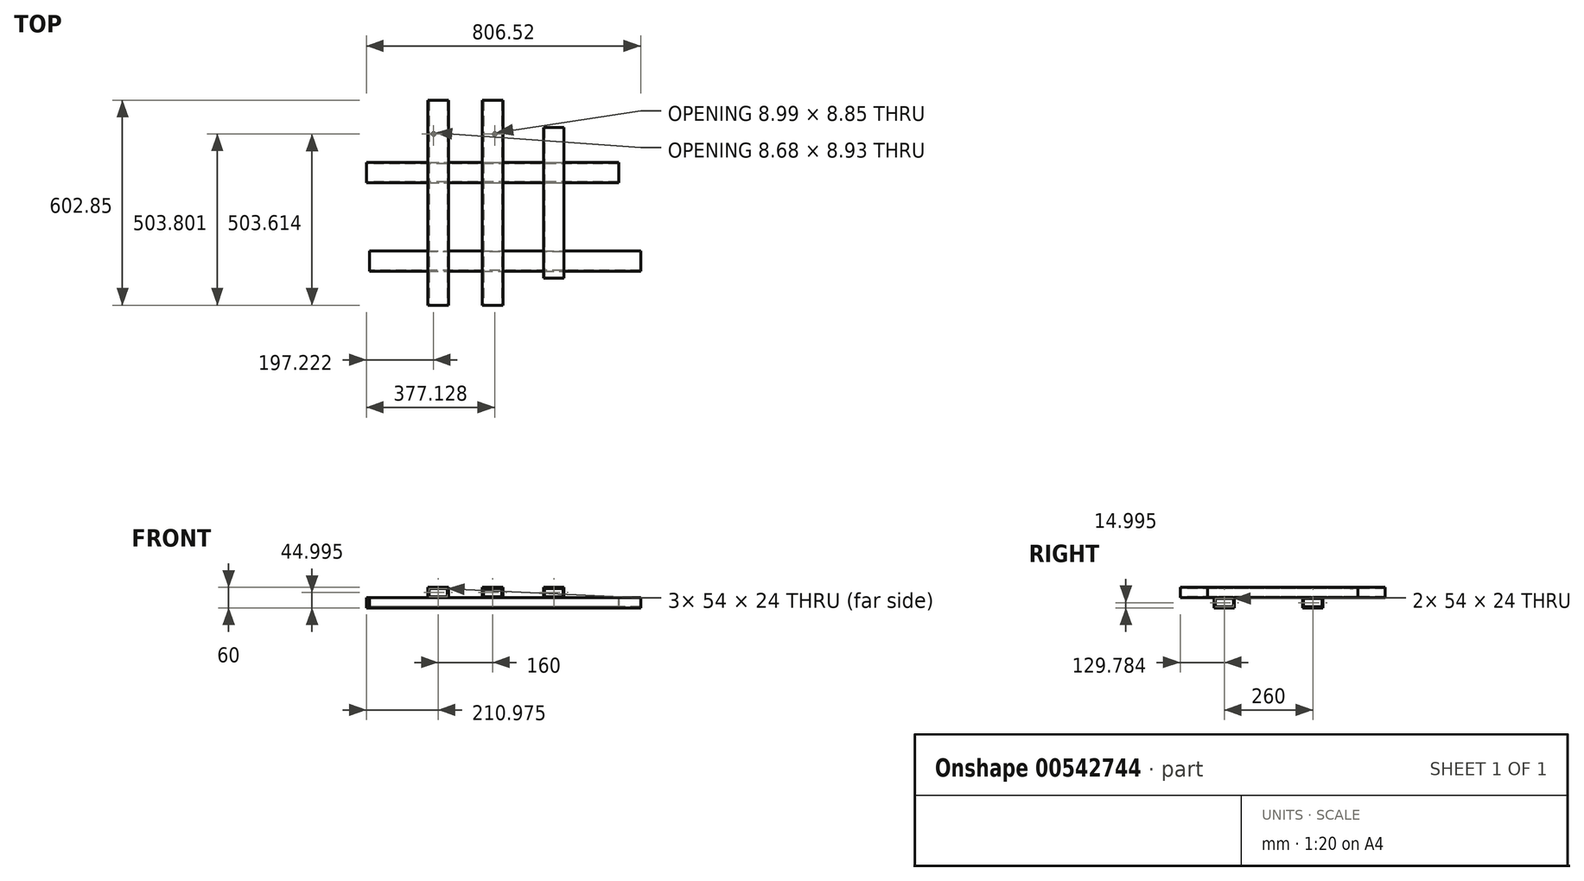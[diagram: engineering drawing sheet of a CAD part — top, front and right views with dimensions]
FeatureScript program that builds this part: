
annotation { "Feature Type Name" : "Feature", "Feature Type Description" : "" }
export const myFeature = defineFeature(function(context is Context, id is Id, definition is map)
    precondition{}
    {
        {
            var Q0;
            Q0=qCreatedBy(makeId("Right.planeOp"),FACE);
            var sketch = newSketch(context, id + "F0", { "sketchPlane" : qUnion([Q0])});
            skLineSegment(sketch, "E0.bottom", {"start": v(-56.7, 72.5) * mm, "end": v(3.3, 72.5) * mm});
            skLineSegment(sketch, "E0.top", {"start": v(-56.7, 42.5) * mm, "end": v(3.3, 42.5) * mm});
            skLineSegment(sketch, "E0.left", {"start": v(-56.7, 72.5) * mm, "end": v(-56.7, 42.5) * mm});
            skLineSegment(sketch, "E0.right", {"start": v(3.3, 72.5) * mm, "end": v(3.3, 42.5) * mm});
            skSolve(sketch);
        }
        {
            var Q0;
            Q0=makeQuery(id+"F0.imprint","IMPRINT",FACE,{"disambiguationData":[TD([[makeQuery(id+"F0.imprint","IMPRINT",EDGE,{"derivedFrom":sQuery(id+"F0.wireOp",EDGE,"E0.bottom")}),-1.0]])]});
            extrude(context, id + "F1", {"entities" : qUnion([Q0]), "depth" : 158 * mm, "offsetDistance" : 25 * mm});
        }
        {
            var Q0;
            Q0=makeQuery(id+"F1.opExtrude","SWEPT_FACE",FACE,{"disambiguationData":[OSD([sQuery(id+"F0.wireOp",EDGE,"E0.left")])]});
            var sketch = newSketch(context, id + "F2", { "sketchPlane" : qUnion([Q0])});
            skLineSegment(sketch, "E1", {"start": v(-144.22, -87.6) * mm, "end": v(237.73, -87.6) * mm, "construction": true});
            skLineSegment(sketch, "E2.bottom", {"start": v(-88.45, -87.6) * mm, "end": v(-22.16, -87.6) * mm});
            skLineSegment(sketch, "E2.top", {"start": v(-88.45, -58.13) * mm, "end": v(-22.16, -58.13) * mm});
            skLineSegment(sketch, "E2.left", {"start": v(-88.45, -87.6) * mm, "end": v(-88.45, -58.13) * mm});
            skLineSegment(sketch, "E2.right", {"start": v(-22.16, -87.6) * mm, "end": v(-22.16, -58.13) * mm});
            skLineSegment(sketch, "E3.bottom", {"start": v(22.03, -87.6) * mm, "end": v(90.42, -87.6) * mm});
            skLineSegment(sketch, "E3.top", {"start": v(22.03, -57.08) * mm, "end": v(90.42, -57.08) * mm});
            skLineSegment(sketch, "E3.left", {"start": v(22.03, -87.6) * mm, "end": v(22.03, -57.08) * mm});
            skLineSegment(sketch, "E3.right", {"start": v(90.42, -87.6) * mm, "end": v(90.42, -57.08) * mm});
            skLineSegment(sketch, "E4.bottom", {"start": v(148.3, -87.6) * mm, "end": v(215.64, -87.6) * mm});
            skLineSegment(sketch, "E4.top", {"start": v(148.3, -57.08) * mm, "end": v(215.64, -57.08) * mm});
            skLineSegment(sketch, "E4.left", {"start": v(148.3, -87.6) * mm, "end": v(148.3, -57.08) * mm});
            skLineSegment(sketch, "E4.right", {"start": v(215.64, -87.6) * mm, "end": v(215.64, -57.08) * mm});
            skSolve(sketch);
        }
        {
            var Q0;
            Q0=makeQuery(id+"F2.imprint","IMPRINT",FACE,{"disambiguationData":[TD([[makeQuery(id+"F2.imprint","IMPRINT",EDGE,{"derivedFrom":sQuery(id+"F2.wireOp",EDGE,"E2.bottom")}),1.0]])]});
            var Q1;
            Q1=makeQuery(id+"F2.imprint","IMPRINT",FACE,{"disambiguationData":[TD([[makeQuery(id+"F2.imprint","IMPRINT",EDGE,{"derivedFrom":sQuery(id+"F2.wireOp",EDGE,"E3.bottom")}),1.0]])]});
            var Q2;
            Q2=makeQuery(id+"F2.imprint","IMPRINT",FACE,{"disambiguationData":[TD([[makeQuery(id+"F2.imprint","IMPRINT",EDGE,{"derivedFrom":sQuery(id+"F2.wireOp",EDGE,"E4.bottom")}),1.0]])]});
            extrude(context, id + "F3", {"entities" : qUnion([Q0, Q1, Q2]), "oppositeDirection" : true, "depth" : 300 * mm, "offsetDistance" : 25 * mm});
        }
        {
            var Q0;
            Q0=makeQuery(id+"F3.opExtrude","SWEPT_FACE",FACE,{"disambiguationData":[OSD([sQuery(id+"F2.wireOp",EDGE,"E2.left")])]});
            var sketch = newSketch(context, id + "F4", { "sketchPlane" : qUnion([Q0])});
            skLineSegment(sketch, "E5.bottom", {"start": v(-213, -87.6) * mm, "end": v(-165.96, -87.6) * mm});
            skLineSegment(sketch, "E5.top", {"start": v(-213, -110.35) * mm, "end": v(-165.96, -110.35) * mm});
            skLineSegment(sketch, "E5.left", {"start": v(-213, -87.6) * mm, "end": v(-213, -110.35) * mm});
            skLineSegment(sketch, "E5.right", {"start": v(-165.96, -87.6) * mm, "end": v(-165.96, -110.35) * mm});
            skLineSegment(sketch, "E6.bottom", {"start": v(-38.67, -87.6) * mm, "end": v(10.72, -87.6) * mm});
            skLineSegment(sketch, "E6.top", {"start": v(-38.67, -111.4) * mm, "end": v(10.72, -111.4) * mm});
            skLineSegment(sketch, "E6.left", {"start": v(-38.67, -87.6) * mm, "end": v(-38.67, -111.4) * mm});
            skLineSegment(sketch, "E6.right", {"start": v(10.72, -87.6) * mm, "end": v(10.72, -111.4) * mm});
            skSolve(sketch);
        }
        {
            var Q0;
            Q0=makeQuery(id+"F4.imprint","IMPRINT",FACE,{"disambiguationData":[TD([[makeQuery(id+"F4.imprint","IMPRINT",EDGE,{"derivedFrom":sQuery(id+"F4.wireOp",EDGE,"E5.bottom")}),-1.0]])]});
            var Q1;
            Q1=makeQuery(id+"F4.imprint","IMPRINT",FACE,{"disambiguationData":[TD([[makeQuery(id+"F4.imprint","IMPRINT",EDGE,{"derivedFrom":sQuery(id+"F4.wireOp",EDGE,"E6.bottom")}),-1.0]])]});
            extrude(context, id + "F5", {"entities" : qUnion([Q0, Q1]), "oppositeDirection" : true, "depth" : 400 * mm, "offsetDistance" : 25 * mm});
        }
        {
            var Q0;
            Q0=makeQuery(id+"F5.opExtrude","CAP_FACE",FACE,{"disambiguationData":[OSD([sQuery(id+"F4.wireOp",EDGE,"E5.bottom"),sQuery(id+"F4.wireOp",EDGE,"E5.top"),sQuery(id+"F4.wireOp",EDGE,"E5.left"),sQuery(id+"F4.wireOp",EDGE,"E5.right")])],"isStart":true});
            var Q1;
            Q1=makeQuery(id+"F5.opExtrude","CAP_FACE",FACE,{"disambiguationData":[OSD([sQuery(id+"F4.wireOp",EDGE,"E6.bottom"),sQuery(id+"F4.wireOp",EDGE,"E6.top"),sQuery(id+"F4.wireOp",EDGE,"E6.left"),sQuery(id+"F4.wireOp",EDGE,"E6.right")])],"isStart":true});
            extrude(context, id + "F6", {"entities" : qUnion([Q0, Q1]), "depth" : 50 * mm, "offsetDistance" : 25 * mm});
        }
        {
            var Q0;
            Q0=makeQuery(id+"F3.opExtrude","CAP_FACE",FACE,{"disambiguationData":[OSD([sQuery(id+"F2.wireOp",EDGE,"E2.bottom"),sQuery(id+"F2.wireOp",EDGE,"E2.top"),sQuery(id+"F2.wireOp",EDGE,"E2.left"),sQuery(id+"F2.wireOp",EDGE,"E2.right")])],"isStart":true});
            var sketch = newSketch(context, id + "F7", { "sketchPlane" : qUnion([Q0])});
            skLineSegment(sketch, "E7.bottom", {"start": v(-85.71, -60.8) * mm, "end": v(-24.6, -60.8) * mm});
            skLineSegment(sketch, "E7.top", {"start": v(-85.71, -84.37) * mm, "end": v(-24.6, -84.37) * mm});
            skLineSegment(sketch, "E7.left", {"start": v(-85.71, -60.8) * mm, "end": v(-85.71, -84.37) * mm});
            skLineSegment(sketch, "E7.right", {"start": v(-24.6, -60.8) * mm, "end": v(-24.6, -84.37) * mm});
            skSolve(sketch);
        }
        {
            var Q0;
            Q0=makeQuery(id+"F7.imprint","IMPRINT",FACE,{"disambiguationData":[TD([[makeQuery(id+"F7.imprint","IMPRINT",EDGE,{"derivedFrom":sQuery(id+"F7.wireOp",EDGE,"E7.bottom")}),-1.0]])]});
            extrude(context, id + "F8", {"entities" : qUnion([Q0]), "operationType" : NewBodyOperationType.REMOVE, "endBound" : BoundingType.UP_TO_NEXT, "oppositeDirection" : true, "depth" : 25 * mm, "offsetDistance" : 25 * mm});
        }
        {
            var Q0;
            Q0=makeQuery(id+"F3.opExtrude","CAP_FACE",FACE,{"disambiguationData":[OSD([sQuery(id+"F2.wireOp",EDGE,"E3.bottom"),sQuery(id+"F2.wireOp",EDGE,"E3.top"),sQuery(id+"F2.wireOp",EDGE,"E3.left"),sQuery(id+"F2.wireOp",EDGE,"E3.right")])],"isStart":true});
            var sketch = newSketch(context, id + "F9", { "sketchPlane" : qUnion([Q0])});
            skLineSegment(sketch, "E8.bottom", {"start": v(25.47, -60.4) * mm, "end": v(87.3, -60.4) * mm});
            skLineSegment(sketch, "E8.top", {"start": v(25.47, -84.14) * mm, "end": v(87.3, -84.14) * mm});
            skLineSegment(sketch, "E8.left", {"start": v(25.47, -60.4) * mm, "end": v(25.47, -84.14) * mm});
            skLineSegment(sketch, "E8.right", {"start": v(87.3, -60.4) * mm, "end": v(87.3, -84.14) * mm});
            skLineSegment(sketch, "E9.bottom", {"start": v(151.6, -60.59) * mm, "end": v(212.25, -60.59) * mm});
            skLineSegment(sketch, "E9.top", {"start": v(151.6, -84.37) * mm, "end": v(212.25, -84.37) * mm});
            skLineSegment(sketch, "E9.left", {"start": v(151.6, -60.59) * mm, "end": v(151.6, -84.37) * mm});
            skLineSegment(sketch, "E9.right", {"start": v(212.25, -60.59) * mm, "end": v(212.25, -84.37) * mm});
            skSolve(sketch);
        }
        {
            var Q0;
            Q0=makeQuery(id+"F9.imprint","IMPRINT",FACE,{"disambiguationData":[TD([[makeQuery(id+"F9.imprint","IMPRINT",EDGE,{"derivedFrom":sQuery(id+"F9.wireOp",EDGE,"E9.bottom")}),-1.0]])]});
            var Q1;
            Q1=makeQuery(id+"F9.imprint","IMPRINT",FACE,{"disambiguationData":[TD([[makeQuery(id+"F9.imprint","IMPRINT",EDGE,{"derivedFrom":sQuery(id+"F9.wireOp",EDGE,"E8.bottom")}),-1.0]])]});
            extrude(context, id + "F10", {"entities" : qUnion([Q0, Q1]), "operationType" : NewBodyOperationType.REMOVE, "endBound" : BoundingType.THROUGH_ALL, "oppositeDirection" : true, "depth" : 25 * mm, "offsetDistance" : 25 * mm});
        }
        {
            var Q0;
            Q0=makeQuery(id+"F3.opExtrude","CAP_FACE",FACE,{"disambiguationData":[OSD([sQuery(id+"F2.wireOp",EDGE,"E3.bottom"),sQuery(id+"F2.wireOp",EDGE,"E3.top"),sQuery(id+"F2.wireOp",EDGE,"E3.left"),sQuery(id+"F2.wireOp",EDGE,"E3.right")])],"isStart":true});
            var sketch = newSketch(context, id + "F11", { "sketchPlane" : qUnion([Q0])});
            skLineSegment(sketch, "E10.bottom", {"start": v(25.35, -60.69) * mm, "end": v(86.6, -60.69) * mm});
            skLineSegment(sketch, "E10.top", {"start": v(25.35, -84.36) * mm, "end": v(86.6, -84.36) * mm});
            skLineSegment(sketch, "E10.left", {"start": v(25.35, -60.69) * mm, "end": v(25.35, -84.36) * mm});
            skLineSegment(sketch, "E10.right", {"start": v(86.6, -60.69) * mm, "end": v(86.6, -84.36) * mm});
            skSolve(sketch);
        }
        {
            var Q0;
            Q0 = qSketchRegion(id + "F11", true);
            extrude(context, id + "F12", {"entities" : qUnion([Q0]), "operationType" : NewBodyOperationType.REMOVE, "endBound" : BoundingType.THROUGH_ALL, "oppositeDirection" : true, "depth" : 25 * mm, "offsetDistance" : 25 * mm});
        }
        {
            var Q0;
            Q0=makeQuery(id+"F5.opExtrude","CAP_FACE",FACE,{"disambiguationData":[OSD([sQuery(id+"F4.wireOp",EDGE,"E6.bottom"),sQuery(id+"F4.wireOp",EDGE,"E6.top"),sQuery(id+"F4.wireOp",EDGE,"E6.left"),sQuery(id+"F4.wireOp",EDGE,"E6.right")])],"isStart":false});
            var sketch = newSketch(context, id + "F13", { "sketchPlane" : qUnion([Q0])});
            skLineSegment(sketch, "E11.bottom", {"start": v(-6.95, -90.73) * mm, "end": v(34.87, -90.73) * mm});
            skLineSegment(sketch, "E11.top", {"start": v(-6.95, -108.67) * mm, "end": v(34.87, -108.67) * mm});
            skLineSegment(sketch, "E11.left", {"start": v(-6.95, -90.73) * mm, "end": v(-6.95, -108.67) * mm});
            skLineSegment(sketch, "E11.right", {"start": v(34.87, -90.73) * mm, "end": v(34.87, -108.67) * mm});
            skSolve(sketch);
        }
        {
            var Q0;
            Q0 = qSketchRegion(id + "F13", true);
            extrude(context, id + "F14", {"entities" : qUnion([Q0]), "operationType" : NewBodyOperationType.REMOVE, "endBound" : BoundingType.THROUGH_ALL, "oppositeDirection" : true, "depth" : 400 * mm, "offsetDistance" : 25 * mm});
        }
        {
            var Q0;
            Q0=makeQuery(id+"F6.opExtrude","CAP_FACE",FACE,{"disambiguationData":[OSD([sQuery(id+"F4.wireOp",EDGE,"E6.bottom"),sQuery(id+"F4.wireOp",EDGE,"E6.top"),sQuery(id+"F4.wireOp",EDGE,"E6.left"),sQuery(id+"F4.wireOp",EDGE,"E6.right")])],"isStart":false});
            var sketch = newSketch(context, id + "F15", { "sketchPlane" : qUnion([Q0])});
            skLineSegment(sketch, "E12.bottom", {"start": v(-35.57, -91.24) * mm, "end": v(7.03, -91.24) * mm});
            skLineSegment(sketch, "E12.top", {"start": v(-35.57, -107.65) * mm, "end": v(7.03, -107.65) * mm});
            skLineSegment(sketch, "E12.left", {"start": v(-35.57, -91.24) * mm, "end": v(-35.57, -107.65) * mm});
            skLineSegment(sketch, "E12.right", {"start": v(7.03, -91.24) * mm, "end": v(7.03, -107.65) * mm});
            skSolve(sketch);
        }
        {
            var Q0;
            Q0=makeQuery(id+"F15.imprint","IMPRINT",FACE,{"disambiguationData":[TD([[makeQuery(id+"F15.imprint","IMPRINT",EDGE,{"derivedFrom":sQuery(id+"F15.wireOp",EDGE,"E12.bottom")}),-1.0]])]});
            extrude(context, id + "F16", {"entities" : qUnion([Q0]), "operationType" : NewBodyOperationType.REMOVE, "endBound" : BoundingType.THROUGH_ALL, "oppositeDirection" : true, "depth" : 25 * mm, "offsetDistance" : 25 * mm});
        }
        {
            var Q0;
            Q0=makeQuery(id+"F3.opExtrude","SWEPT_BODY",BODY,{"disambiguationData":[OSD([sQuery(id+"F2.wireOp",EDGE,"E2.bottom"),sQuery(id+"F2.wireOp",EDGE,"E2.top"),sQuery(id+"F2.wireOp",EDGE,"E2.left"),sQuery(id+"F2.wireOp",EDGE,"E2.right")])]});
            var Q1;
            Q1=makeQuery(id+"F3.opExtrude","SWEPT_BODY",BODY,{"disambiguationData":[OSD([sQuery(id+"F2.wireOp",EDGE,"E3.bottom"),sQuery(id+"F2.wireOp",EDGE,"E3.top"),sQuery(id+"F2.wireOp",EDGE,"E3.left"),sQuery(id+"F2.wireOp",EDGE,"E3.right")])]});
            var Q2;
            Q2=makeQuery(id+"F3.opExtrude","SWEPT_BODY",BODY,{"disambiguationData":[OSD([sQuery(id+"F2.wireOp",EDGE,"E4.bottom"),sQuery(id+"F2.wireOp",EDGE,"E4.top"),sQuery(id+"F2.wireOp",EDGE,"E4.left"),sQuery(id+"F2.wireOp",EDGE,"E4.right")])]});
            var Q3;
            Q3=makeQuery(id+"F5.opExtrude","SWEPT_BODY",BODY,{"disambiguationData":[OSD([sQuery(id+"F4.wireOp",EDGE,"E5.bottom"),sQuery(id+"F4.wireOp",EDGE,"E5.top"),sQuery(id+"F4.wireOp",EDGE,"E5.left"),sQuery(id+"F4.wireOp",EDGE,"E5.right")])]});
            var Q4;
            Q4=makeQuery(id+"F5.opExtrude","SWEPT_BODY",BODY,{"disambiguationData":[OSD([sQuery(id+"F4.wireOp",EDGE,"E6.bottom"),sQuery(id+"F4.wireOp",EDGE,"E6.top"),sQuery(id+"F4.wireOp",EDGE,"E6.left"),sQuery(id+"F4.wireOp",EDGE,"E6.right")])]});
            var Q5;
            Q5=makeQuery(id+"F6.opExtrude","SWEPT_BODY",BODY,{"disambiguationData":[OSD([sQuery(id+"F4.wireOp",EDGE,"E5.bottom"),sQuery(id+"F4.wireOp",EDGE,"E5.top"),sQuery(id+"F4.wireOp",EDGE,"E5.left"),sQuery(id+"F4.wireOp",EDGE,"E5.right")])]});
            var Q6;
            Q6=makeQuery(id+"F6.opExtrude","SWEPT_BODY",BODY,{"disambiguationData":[OSD([sQuery(id+"F4.wireOp",EDGE,"E6.bottom"),sQuery(id+"F4.wireOp",EDGE,"E6.top"),sQuery(id+"F4.wireOp",EDGE,"E6.left"),sQuery(id+"F4.wireOp",EDGE,"E6.right")])]});
            deleteBodies(context, id + "F17", {"entities" : qUnion([Q0, Q1, Q2, Q3, Q4, Q5, Q6])});
        }
        {
            var Q0;
            Q0=makeQuery(id+"F1.opExtrude","SWEPT_FACE",FACE,{"disambiguationData":[OSD([sQuery(id+"F0.wireOp",EDGE,"E0.bottom")])]});
            var sketch = newSketch(context, id + "F18", { "sketchPlane" : qUnion([Q0])});
            skCircle(sketch, "E13", {"center": v(62.85, -9.23) * mm, "radius": 8.07 * mm});
            skCircle(sketch, "E14", {"center": v(59.1, -6.9) * mm, "radius": 2.27 * mm});
            skSolve(sketch);
        }
        {
            var Q0;
            Q0=makeQuery(id+"F18.imprint","IMPRINT",FACE,{"disambiguationData":[TD([[makeQuery(id+"F18.imprint","IMPRINT",EDGE,{"derivedFrom":sQuery(id+"F18.wireOp",EDGE,"E13")}),1.0]])]});
            extrude(context, id + "F19", {"entities" : qUnion([Q0]), "depth" : 10 * mm, "offsetDistance" : 25 * mm});
        }
        {
            var Q0;
            Q0=makeQuery(id+"F1.opExtrude","SWEPT_FACE",FACE,{"disambiguationData":[OSD([sQuery(id+"F0.wireOp",EDGE,"E0.bottom")])]});
            var sketch = newSketch(context, id + "F20", { "sketchPlane" : qUnion([Q0])});
            skLineSegment(sketch, "E15", {"start": v(-511.42, -56.84) * mm, "end": v(-73.93, -56.84) * mm, "construction": true});
            skSolve(sketch);
        }
        {
            var Q0;
            {var subQ0=sQuery(id+"F0.wireOp",EDGE,"E0.bottom");Q0=makeQuery(id+"F20.imprint","IMPRINT",FACE,{"disambiguationData":[TD([[makeQuery(id+"F20.imprint","IMPRINT",EDGE,{"derivedFrom":makeQuery(id+"F1.opExtrude","CAP_EDGE",EDGE,{"disambiguationData":[OSD([subQ0])],"isStart":true})}),-1.0]])]});}
            var sketch = newSketch(context, id + "F21", { "sketchPlane" : qUnion([Q0])});
            skLineSegment(sketch, "E16.bottom", {"start": v(-538.91, 244.36) * mm, "end": v(-478.91, 244.36) * mm});
            skLineSegment(sketch, "E16.top", {"start": v(-538.91, -358.5) * mm, "end": v(-478.91, -358.5) * mm});
            skLineSegment(sketch, "E16.left", {"start": v(-538.91, 244.36) * mm, "end": v(-538.91, -358.5) * mm});
            skLineSegment(sketch, "E16.right", {"start": v(-478.91, 244.36) * mm, "end": v(-478.91, -358.5) * mm});
            skPoint(sketch, "E16.middle", {"position": v(-508.91, -57.06) * mm});
            skLineSegment(sketch, "E17.bottom", {"start": v(-378.91, 244.36) * mm, "end": v(-318.91, 244.36) * mm});
            skLineSegment(sketch, "E17.top", {"start": v(-378.91, -358.5) * mm, "end": v(-318.91, -358.5) * mm});
            skLineSegment(sketch, "E17.left", {"start": v(-378.91, 244.36) * mm, "end": v(-378.91, -358.5) * mm});
            skLineSegment(sketch, "E17.right", {"start": v(-318.91, 244.36) * mm, "end": v(-318.91, -358.5) * mm});
            skPoint(sketch, "E17.middle", {"position": v(-348.91, -57.06) * mm});
            skLineSegment(sketch, "E18.bottom", {"start": v(-198.91, 164.36) * mm, "end": v(-138.91, 164.36) * mm});
            skLineSegment(sketch, "E18.top", {"start": v(-198.91, -278.5) * mm, "end": v(-138.91, -278.5) * mm});
            skLineSegment(sketch, "E18.left", {"start": v(-198.91, 164.36) * mm, "end": v(-198.91, -278.5) * mm});
            skLineSegment(sketch, "E18.right", {"start": v(-138.91, 164.36) * mm, "end": v(-138.91, -278.5) * mm});
            skPoint(sketch, "E18.middle", {"position": v(-168.91, -57.06) * mm});
            skLineSegment(sketch, "E19.bottom", {"start": v(-618.64, 67.1) * mm, "end": v(35.81, 67.1) * mm});
            skLineSegment(sketch, "E19.top", {"start": v(-618.64, 7.1) * mm, "end": v(35.81, 7.1) * mm});
            skLineSegment(sketch, "E19.left", {"start": v(-618.64, 67.1) * mm, "end": v(-618.64, 7.1) * mm});
            skLineSegment(sketch, "E19.right", {"start": v(35.81, 67.1) * mm, "end": v(35.81, 7.1) * mm});
            skLineSegment(sketch, "E20.bottom", {"start": v(-614.19, -172.9) * mm, "end": v(35.81, -172.9) * mm});
            skLineSegment(sketch, "E20.top", {"start": v(-614.19, -232.9) * mm, "end": v(35.81, -232.9) * mm});
            skLineSegment(sketch, "E20.left", {"start": v(-614.19, -172.9) * mm, "end": v(-614.19, -232.9) * mm});
            skLineSegment(sketch, "E20.right", {"start": v(35.81, -172.9) * mm, "end": v(35.81, -232.9) * mm});
            skSolve(sketch);
        }
        {
            var Q0;
            {var subQ0=sQuery(id+"F21.wireOp",EDGE,"E16.bottom");Q0=makeQuery(id+"F21.imprint","IMPRINT",FACE,{"disambiguationData":[TD([[makeQuery(id+"F21.imprint","IMPRINT",EDGE,{"derivedFrom":subQ0}),-1.0]])]});}
            var Q1;
            {var subQ0=sQuery(id+"F21.wireOp",EDGE,"E19.bottom");var subQ1=sQuery(id+"F21.wireOp",EDGE,"E16.left");var subQ2=makeQuery(id+"F21.imprint","INTERSECT",VERTEX,{"derivedFrom":[subQ1,subQ0]});Q1=makeQuery(id+"F21.imprint","IMPRINT",FACE,{"disambiguationData":[TD([[makeQuery(id+"F21.imprint","IMPRINT",EDGE,{"disambiguationData":[TD([[subQ2,-1.0]])],"derivedFrom":subQ1}),1.0]])]});}
            var Q2;
            {var subQ0=sQuery(id+"F21.wireOp",EDGE,"E19.top");var subQ1=sQuery(id+"F21.wireOp",EDGE,"E16.left");var subQ2=makeQuery(id+"F21.imprint","INTERSECT",VERTEX,{"derivedFrom":[subQ1,subQ0]});Q2=makeQuery(id+"F21.imprint","IMPRINT",FACE,{"disambiguationData":[TD([[makeQuery(id+"F21.imprint","IMPRINT",EDGE,{"disambiguationData":[TD([[subQ2,-1.0]])],"derivedFrom":subQ1}),1.0]])]});}
            var Q3;
            {var subQ0=sQuery(id+"F21.wireOp",EDGE,"E20.bottom");var subQ1=sQuery(id+"F21.wireOp",EDGE,"E16.left");var subQ2=makeQuery(id+"F21.imprint","INTERSECT",VERTEX,{"derivedFrom":[subQ1,subQ0]});Q3=makeQuery(id+"F21.imprint","IMPRINT",FACE,{"disambiguationData":[TD([[makeQuery(id+"F21.imprint","IMPRINT",EDGE,{"disambiguationData":[TD([[subQ2,-1.0]])],"derivedFrom":subQ1}),1.0]])]});}
            var Q4;
            {var subQ0=sQuery(id+"F21.wireOp",EDGE,"E16.top");Q4=makeQuery(id+"F21.imprint","IMPRINT",FACE,{"disambiguationData":[TD([[makeQuery(id+"F21.imprint","IMPRINT",EDGE,{"derivedFrom":subQ0}),1.0]])]});}
            var Q5;
            {var subQ0=sQuery(id+"F21.wireOp",EDGE,"E17.top");Q5=makeQuery(id+"F21.imprint","IMPRINT",FACE,{"disambiguationData":[TD([[makeQuery(id+"F21.imprint","IMPRINT",EDGE,{"derivedFrom":subQ0}),1.0]])]});}
            var Q6;
            {var subQ0=sQuery(id+"F21.wireOp",EDGE,"E20.top");var subQ1=sQuery(id+"F21.wireOp",EDGE,"E17.left");var subQ2=makeQuery(id+"F21.imprint","INTERSECT",VERTEX,{"derivedFrom":[subQ1,subQ0]});Q6=makeQuery(id+"F21.imprint","IMPRINT",FACE,{"disambiguationData":[TD([[makeQuery(id+"F21.imprint","IMPRINT",EDGE,{"disambiguationData":[TD([[subQ2,1.0]])],"derivedFrom":subQ1}),1.0]])]});}
            var Q7;
            {var subQ0=sQuery(id+"F21.wireOp",EDGE,"E19.top");var subQ1=sQuery(id+"F21.wireOp",EDGE,"E17.left");var subQ2=makeQuery(id+"F21.imprint","INTERSECT",VERTEX,{"derivedFrom":[subQ1,subQ0]});Q7=makeQuery(id+"F21.imprint","IMPRINT",FACE,{"disambiguationData":[TD([[makeQuery(id+"F21.imprint","IMPRINT",EDGE,{"disambiguationData":[TD([[subQ2,-1.0]])],"derivedFrom":subQ1}),1.0]])]});}
            var Q8;
            {var subQ0=sQuery(id+"F21.wireOp",EDGE,"E19.bottom");var subQ1=sQuery(id+"F21.wireOp",EDGE,"E17.left");var subQ2=makeQuery(id+"F21.imprint","INTERSECT",VERTEX,{"derivedFrom":[subQ1,subQ0]});Q8=makeQuery(id+"F21.imprint","IMPRINT",FACE,{"disambiguationData":[TD([[makeQuery(id+"F21.imprint","IMPRINT",EDGE,{"disambiguationData":[TD([[subQ2,-1.0]])],"derivedFrom":subQ1}),1.0]])]});}
            var Q9;
            {var subQ0=sQuery(id+"F21.wireOp",EDGE,"E17.bottom");Q9=makeQuery(id+"F21.imprint","IMPRINT",FACE,{"disambiguationData":[TD([[makeQuery(id+"F21.imprint","IMPRINT",EDGE,{"derivedFrom":subQ0}),-1.0]])]});}
            var Q10;
            {var subQ0=sQuery(id+"F21.wireOp",EDGE,"E18.bottom");Q10=makeQuery(id+"F21.imprint","IMPRINT",FACE,{"disambiguationData":[TD([[makeQuery(id+"F21.imprint","IMPRINT",EDGE,{"derivedFrom":subQ0}),-1.0]])]});}
            var Q11;
            {var subQ0=sQuery(id+"F21.wireOp",EDGE,"E19.bottom");var subQ1=sQuery(id+"F21.wireOp",EDGE,"E18.left");var subQ2=makeQuery(id+"F21.imprint","INTERSECT",VERTEX,{"derivedFrom":[subQ1,subQ0]});Q11=makeQuery(id+"F21.imprint","IMPRINT",FACE,{"disambiguationData":[TD([[makeQuery(id+"F21.imprint","IMPRINT",EDGE,{"disambiguationData":[TD([[subQ2,-1.0]])],"derivedFrom":subQ1}),1.0]])]});}
            var Q12;
            {var subQ0=sQuery(id+"F21.wireOp",EDGE,"E19.top");var subQ1=sQuery(id+"F21.wireOp",EDGE,"E18.left");var subQ2=makeQuery(id+"F21.imprint","INTERSECT",VERTEX,{"derivedFrom":[subQ1,subQ0]});Q12=makeQuery(id+"F21.imprint","IMPRINT",FACE,{"disambiguationData":[TD([[makeQuery(id+"F21.imprint","IMPRINT",EDGE,{"disambiguationData":[TD([[subQ2,-1.0]])],"derivedFrom":subQ1}),1.0]])]});}
            var Q13;
            {var subQ0=sQuery(id+"F21.wireOp",EDGE,"E20.top");var subQ1=sQuery(id+"F21.wireOp",EDGE,"E18.left");var subQ2=makeQuery(id+"F21.imprint","INTERSECT",VERTEX,{"derivedFrom":[subQ1,subQ0]});Q13=makeQuery(id+"F21.imprint","IMPRINT",FACE,{"disambiguationData":[TD([[makeQuery(id+"F21.imprint","IMPRINT",EDGE,{"disambiguationData":[TD([[subQ2,1.0]])],"derivedFrom":subQ1}),1.0]])]});}
            var Q14;
            {var subQ0=sQuery(id+"F21.wireOp",EDGE,"E18.top");Q14=makeQuery(id+"F21.imprint","IMPRINT",FACE,{"disambiguationData":[TD([[makeQuery(id+"F21.imprint","IMPRINT",EDGE,{"derivedFrom":subQ0}),1.0]])]});}
            extrude(context, id + "F22", {"entities" : qUnion([Q0, Q1, Q2, Q3, Q4, Q5, Q6, Q7, Q8, Q9, Q10, Q11, Q12, Q13, Q14]), "depth" : 30 * mm, "offsetDistance" : 25 * mm});
        }
        {
            var Q0;
            Q0=makeQuery(id+"F22.opExtrude","CAP_FACE",FACE,{"disambiguationData":[OSD([sQuery(id+"F21.wireOp",EDGE,"E16.bottom"),sQuery(id+"F21.wireOp",EDGE,"E16.top"),sQuery(id+"F21.wireOp",EDGE,"E16.left"),sQuery(id+"F21.wireOp",EDGE,"E16.right")])],"isStart":true});
            var sketch = newSketch(context, id + "F23", { "sketchPlane" : qUnion([Q0])});
            skLineSegment(sketch, "E21.bottom", {"start": v(-710.84, 258.7) * mm, "end": v(86.63, 258.7) * mm});
            skLineSegment(sketch, "E21.top", {"start": v(-710.84, 198.7) * mm, "end": v(86.63, 198.7) * mm});
            skLineSegment(sketch, "E21.left", {"start": v(-710.84, 258.7) * mm, "end": v(-710.84, 198.7) * mm});
            skLineSegment(sketch, "E21.right", {"start": v(86.63, 258.7) * mm, "end": v(86.63, 198.7) * mm});
            skLineSegment(sketch, "E22.bottom", {"start": v(-719.89, -1.3) * mm, "end": v(106.26, -1.3) * mm});
            skLineSegment(sketch, "E22.top", {"start": v(-719.89, -61.3) * mm, "end": v(106.26, -61.3) * mm});
            skLineSegment(sketch, "E22.left", {"start": v(-719.89, -1.3) * mm, "end": v(-719.89, -61.3) * mm});
            skLineSegment(sketch, "E22.right", {"start": v(106.26, -1.3) * mm, "end": v(106.26, -61.3) * mm});
            skSolve(sketch);
        }
        {
            var Q0;
            Q0 = qSketchRegion(id + "F23", true);
            extrude(context, id + "F24", {"entities" : qUnion([Q0]), "depth" : 30 * mm, "offsetDistance" : 25 * mm});
        }
        {
            var Q0;
            Q0=makeQuery(id+"F24.opExtrude","SWEPT_FACE",FACE,{"disambiguationData":[OSD([sQuery(id+"F23.wireOp",EDGE,"E22.left")])]});
            var sketch = newSketch(context, id + "F25", { "sketchPlane" : qUnion([Q0])});
            skLineSegment(sketch, "E23.0", {"start": v(-4.3, 69.5) * mm, "end": v(-58.3, 69.5) * mm});
            skLineSegment(sketch, "E23.1", {"start": v(-4.3, 45.5) * mm, "end": v(-4.3, 69.5) * mm});
            skLineSegment(sketch, "E23.2", {"start": v(-58.3, 45.5) * mm, "end": v(-4.3, 45.5) * mm});
            skLineSegment(sketch, "E23.3", {"start": v(-58.3, 69.5) * mm, "end": v(-58.3, 45.5) * mm});
            skSolve(sketch);
        }
        {
            var Q0;
            Q0=makeQuery(id+"F25.imprint","IMPRINT",FACE,{"disambiguationData":[TD([[makeQuery(id+"F25.imprint","IMPRINT",EDGE,{"derivedFrom":sQuery(id+"F25.wireOp",EDGE,"E23.0")}),1.0]])]});
            extrude(context, id + "F26", {"entities" : qUnion([Q0]), "operationType" : NewBodyOperationType.REMOVE, "endBound" : BoundingType.THROUGH_ALL, "oppositeDirection" : true, "depth" : 25 * mm, "offsetDistance" : 25 * mm});
        }
        {
            var Q0;
            Q0=makeQuery(id+"F24.opExtrude","SWEPT_FACE",FACE,{"disambiguationData":[OSD([sQuery(id+"F23.wireOp",EDGE,"E21.left")])]});
            var sketch = newSketch(context, id + "F27", { "sketchPlane" : qUnion([Q0])});
            skLineSegment(sketch, "E24.0", {"start": v(255.7, 69.5) * mm, "end": v(201.7, 69.5) * mm});
            skLineSegment(sketch, "E24.1", {"start": v(255.7, 45.5) * mm, "end": v(255.7, 69.5) * mm});
            skLineSegment(sketch, "E24.2", {"start": v(201.7, 45.5) * mm, "end": v(255.7, 45.5) * mm});
            skLineSegment(sketch, "E24.3", {"start": v(201.7, 69.5) * mm, "end": v(201.7, 45.5) * mm});
            skSolve(sketch);
        }
        {
            var Q0;
            Q0 = qSketchRegion(id + "F27", true);
            extrude(context, id + "F28", {"entities" : qUnion([Q0]), "operationType" : NewBodyOperationType.REMOVE, "endBound" : BoundingType.THROUGH_ALL, "oppositeDirection" : true, "depth" : 25 * mm, "offsetDistance" : 25 * mm});
        }
        {
            var Q0;
            Q0=makeQuery(id+"F22.opExtrude","SWEPT_FACE",FACE,{"disambiguationData":[OSD([sQuery(id+"F21.wireOp",EDGE,"E16.top")])]});
            var sketch = newSketch(context, id + "F29", { "sketchPlane" : qUnion([Q0])});
            skLineSegment(sketch, "E25.0", {"start": v(-535.91, 75.5) * mm, "end": v(-481.91, 75.5) * mm});
            skLineSegment(sketch, "E25.1", {"start": v(-535.91, 99.5) * mm, "end": v(-535.91, 75.5) * mm});
            skLineSegment(sketch, "E25.2", {"start": v(-481.91, 99.5) * mm, "end": v(-535.91, 99.5) * mm});
            skLineSegment(sketch, "E25.3", {"start": v(-481.91, 75.5) * mm, "end": v(-481.91, 99.5) * mm});
            skSolve(sketch);
        }
        {
            var Q0;
            Q0=makeQuery(id+"F29.imprint","IMPRINT",FACE,{"disambiguationData":[TD([[makeQuery(id+"F29.imprint","IMPRINT",EDGE,{"derivedFrom":sQuery(id+"F29.wireOp",EDGE,"E25.0")}),1.0]])]});
            extrude(context, id + "F30", {"entities" : qUnion([Q0]), "operationType" : NewBodyOperationType.REMOVE, "endBound" : BoundingType.THROUGH_ALL, "oppositeDirection" : true, "depth" : 25 * mm, "offsetDistance" : 25 * mm});
        }
        {
            var Q0;
            Q0=makeQuery(id+"F22.opExtrude","SWEPT_FACE",FACE,{"disambiguationData":[OSD([sQuery(id+"F21.wireOp",EDGE,"E17.top")])]});
            var sketch = newSketch(context, id + "F31", { "sketchPlane" : qUnion([Q0])});
            skLineSegment(sketch, "E26.0", {"start": v(-375.91, 75.5) * mm, "end": v(-321.91, 75.5) * mm});
            skLineSegment(sketch, "E26.1", {"start": v(-375.91, 99.5) * mm, "end": v(-375.91, 75.5) * mm});
            skLineSegment(sketch, "E26.2", {"start": v(-321.91, 99.5) * mm, "end": v(-375.91, 99.5) * mm});
            skLineSegment(sketch, "E26.3", {"start": v(-321.91, 75.5) * mm, "end": v(-321.91, 99.5) * mm});
            skSolve(sketch);
        }
        {
            var Q0;
            Q0=makeQuery(id+"F31.imprint","IMPRINT",FACE,{"disambiguationData":[TD([[makeQuery(id+"F31.imprint","IMPRINT",EDGE,{"derivedFrom":sQuery(id+"F31.wireOp",EDGE,"E26.0")}),1.0]])]});
            extrude(context, id + "F32", {"entities" : qUnion([Q0]), "operationType" : NewBodyOperationType.REMOVE, "endBound" : BoundingType.THROUGH_ALL, "oppositeDirection" : true, "depth" : 25 * mm, "offsetDistance" : 25 * mm});
        }
        {
            var Q0;
            Q0=makeQuery(id+"F22.opExtrude","SWEPT_FACE",FACE,{"disambiguationData":[OSD([sQuery(id+"F21.wireOp",EDGE,"E18.top")])]});
            var sketch = newSketch(context, id + "F33", { "sketchPlane" : qUnion([Q0])});
            skLineSegment(sketch, "E27.0", {"start": v(-195.91, 75.5) * mm, "end": v(-141.91, 75.5) * mm});
            skLineSegment(sketch, "E27.1", {"start": v(-195.91, 99.5) * mm, "end": v(-195.91, 75.5) * mm});
            skLineSegment(sketch, "E27.2", {"start": v(-141.91, 99.5) * mm, "end": v(-195.91, 99.5) * mm});
            skLineSegment(sketch, "E27.3", {"start": v(-141.91, 75.5) * mm, "end": v(-141.91, 99.5) * mm});
            skSolve(sketch);
        }
        {
            var Q0;
            Q0 = qSketchRegion(id + "F33", true);
            extrude(context, id + "F34", {"entities" : qUnion([Q0]), "operationType" : NewBodyOperationType.REMOVE, "endBound" : BoundingType.THROUGH_ALL, "oppositeDirection" : true, "depth" : 25 * mm, "offsetDistance" : 25 * mm});
        }
        {
            var Q0;
            Q0=makeQuery(id+"F24.opExtrude","SWEPT_FACE",FACE,{"disambiguationData":[OSD([sQuery(id+"F23.wireOp",EDGE,"E22.right")])]});
            extrude(context, id + "F35", {"entities" : qUnion([Q0]), "operationType" : NewBodyOperationType.REMOVE, "oppositeDirection" : true, "depth" : 153.3 * mm, "offsetDistance" : 25 * mm});
        }
        {
            var Q0;
            Q0=makeQuery(id+"F19.opExtrude","SWEPT_BODY",BODY,{"disambiguationData":[OSD([sQuery(id+"F18.wireOp",EDGE,"E13"),sQuery(id+"F18.wireOp",EDGE,"E14")])]});
            var Q1;
            Q1=qCreatedBy(id+"FhlvQuW1xJWPwEq_1.opHelix",BODY);
            var Q2;
            Q2=makeQuery(id+"F1.opExtrude","SWEPT_BODY",BODY,{"disambiguationData":[OSD([sQuery(id+"F0.wireOp",EDGE,"E0.bottom"),sQuery(id+"F0.wireOp",EDGE,"E0.top"),sQuery(id+"F0.wireOp",EDGE,"E0.left"),sQuery(id+"F0.wireOp",EDGE,"E0.right")])]});
            deleteBodies(context, id + "F36", {"entities" : qUnion([Q0, Q1, Q2])});
        }
        {
            var Q0;
            Q0=makeQuery(id+"F35.boolean.opBoolean","COPY",FACE,{"derivedFrom":makeQuery(id+"F35.opExtrude","CAP_FACE",FACE,{"disambiguationData":[OSD([sQuery(id+"F23.wireOp",EDGE,"E22.right")])],"isStart":false})});
            extrude(context, id + "F37", {"entities" : qUnion([Q0]), "operationType" : NewBodyOperationType.ADD, "depth" : 68.6 * mm, "offsetDistance" : 25 * mm});
        }
        {
            var Q0;
            Q0=makeQuery(id+"F22.opExtrude","CAP_FACE",FACE,{"disambiguationData":[OSD([sQuery(id+"F21.wireOp",EDGE,"E16.bottom"),sQuery(id+"F21.wireOp",EDGE,"E16.top"),sQuery(id+"F21.wireOp",EDGE,"E16.left"),sQuery(id+"F21.wireOp",EDGE,"E16.right")])],"isStart":false});
            var sketch = newSketch(context, id + "F38", { "sketchPlane" : qUnion([Q0])});
            skPoint(sketch, "E28", {"position": v(-522.65, 145.19) * mm});
            skPoint(sketch, "E29", {"position": v(-522.65, -44.81) * mm});
            skPoint(sketch, "E30", {"position": v(-342.65, 145.19) * mm});
            skPoint(sketch, "E31", {"position": v(-342.65, -44.81) * mm});
            skSolve(sketch);
        }
        {
            var Q0;
            Q0=makeQuery(id+"F38.imprint","IMPRINT",FACE,{"disambiguationData":[TD([[makeQuery(id+"F38.imprint","IMPRINT",EDGE,{"derivedFrom":makeQuery(id+"F22.opExtrude","CAP_EDGE",EDGE,{"disambiguationData":[OSD([sQuery(id+"F21.wireOp",EDGE,"E16.bottom")])],"isStart":false})}),-1.0]])]});
            var sketch = newSketch(context, id + "F39", { "sketchPlane" : qUnion([Q0])});
            skCircle(sketch, "E32", {"center": v(-522.69, 145.44) * mm, "radius": 4.25 * mm});
            skCircle(sketch, "E33", {"center": v(-342.88, 145.06) * mm, "radius": 4.25 * mm});
            skSolve(sketch);
        }
        {
            var Q0;
            Q0=sQuery(id+"F38.wireOp",VERTEX,"E28");
            var Q1;
            Q1=sQuery(id+"F38.wireOp",VERTEX,"E30");
            var Q2;
            Q2=makeQuery(id+"F22.opExtrude","SWEPT_BODY",BODY,{"disambiguationData":[OSD([sQuery(id+"F21.wireOp",EDGE,"E16.bottom"),sQuery(id+"F21.wireOp",EDGE,"E16.top"),sQuery(id+"F21.wireOp",EDGE,"E16.left"),sQuery(id+"F21.wireOp",EDGE,"E16.right")])]});
            var Q3;
            Q3=makeQuery(id+"F22.opExtrude","SWEPT_BODY",BODY,{"disambiguationData":[OSD([sQuery(id+"F21.wireOp",EDGE,"E17.bottom"),sQuery(id+"F21.wireOp",EDGE,"E17.top"),sQuery(id+"F21.wireOp",EDGE,"E17.left"),sQuery(id+"F21.wireOp",EDGE,"E17.right")])]});
            hole(context, id + "F40", {"style" : HoleStyle.SIMPLE, "endStyle" : HoleEndStyle.BLIND, "standardTappedOrClearance" : lookupTablePath({ "standard" : "ISO", "size" : "8.8", "type" : "Drilled" }), "standardBlindInLast" : lookupTablePath({ "standard" : "ISO", "size" : "8.8", "type" : "Drilled" }), "holeDiameter" : 8.8 * mm, "holeDepth" : 16.5 * mm, "isTappedThrough" : true, "tappedDepth" : 12 * mm, "tapClearance" : 3, "startFromSketch" : true, "locations" : qUnion([Q0, Q1]), "scope" : qUnion([Q2, Q3])});
        }
        {
            var Q0;
            Q0=sQuery(id+"F39.wireOp",VERTEX,"E32.center");
            var Q1;
            Q1=sQuery(id+"F39.wireOp",VERTEX,"E33.center");
            var Q2;
            Q2=makeQuery(id+"F22.opExtrude","SWEPT_BODY",BODY,{"disambiguationData":[OSD([sQuery(id+"F21.wireOp",EDGE,"E16.bottom"),sQuery(id+"F21.wireOp",EDGE,"E16.top"),sQuery(id+"F21.wireOp",EDGE,"E16.left"),sQuery(id+"F21.wireOp",EDGE,"E16.right")])]});
            var Q3;
            Q3=makeQuery(id+"F22.opExtrude","SWEPT_BODY",BODY,{"disambiguationData":[OSD([sQuery(id+"F21.wireOp",EDGE,"E17.bottom"),sQuery(id+"F21.wireOp",EDGE,"E17.top"),sQuery(id+"F21.wireOp",EDGE,"E17.left"),sQuery(id+"F21.wireOp",EDGE,"E17.right")])]});
            hole(context, id + "F41", {"style" : HoleStyle.SIMPLE, "endStyle" : HoleEndStyle.BLIND, "standardTappedOrClearance" : lookupTablePath({ "standard" : "ISO", "size" : "8.8", "type" : "Drilled" }), "standardBlindInLast" : lookupTablePath({ "standard" : "ISO", "size" : "8.8", "type" : "Drilled" }), "holeDiameter" : 8.8 * mm, "holeDepth" : 16.5 * mm, "isTappedThrough" : true, "tappedDepth" : 12 * mm, "tapClearance" : 3, "startFromSketch" : true, "locations" : qUnion([Q0, Q1]), "scope" : qUnion([Q2, Q3])});
        }
    });
